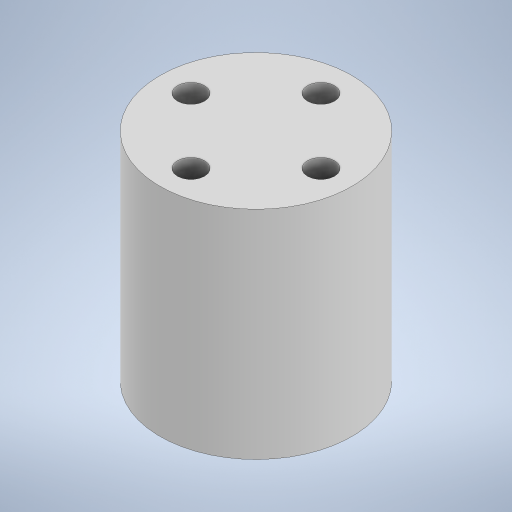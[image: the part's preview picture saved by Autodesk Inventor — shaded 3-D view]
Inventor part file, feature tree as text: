
AUTODESK INVENTOR PART (.ipt)
format: ipt  version: 2024 (Build 280153000, 153)  size: 211,456 bytes
history: native  units: in
note: dims shown in document units (in); Inventor stores cm internally (conversion verified against a paired STEP export)
features: extrude x2, sketch x2
ambient origin geometry x8: Origin, YZ Plane, XZ Plane, XY Plane, X Axis, Y Axis, Z Axis, Center Point
bodies: Solid1 (feature_tree)
feature tree (4):
  extrude  "Extrusion1"  Depth=2.0in TaperAngle=0.0deg
  extrude  "Extrusion3"  TaperAngle=0.0deg  [1 undecoded]
  sketch  "Sketch1"  dims[d0=1.772in d1=2.0in d2=0.0in]
  sketch  "Sketch4"  dims[d6=0.25in d7=0.0in d8=0.6in d9=1.5748in d11=360.0deg d13=1.0in d14=0.0in]
note: 1 required parameter value undecoded (feature->parameter linkage not recoverable at this tier; creation-order binding heuristic only, values carry confidence <= 0.55)
